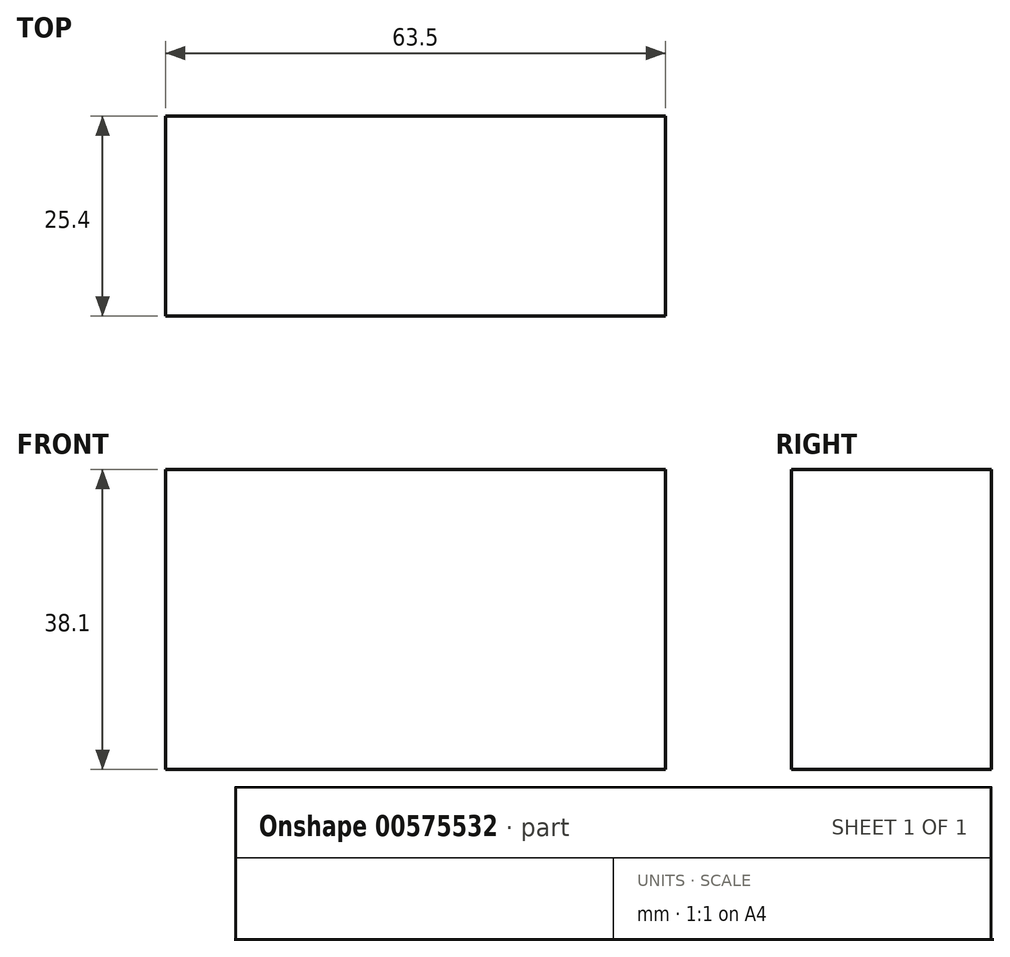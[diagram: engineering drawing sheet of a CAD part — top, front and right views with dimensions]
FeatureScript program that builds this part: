
annotation { "Feature Type Name" : "Feature", "Feature Type Description" : "" }
export const myFeature = defineFeature(function(context is Context, id is Id, definition is map)
    precondition{}
    {
        {
            var Q0;
            Q0=qCreatedBy(makeId("Front.planeOp"),FACE);
            var sketch = newSketch(context, id + "F0", { "sketchPlane" : qUnion([Q0])});
            skLineSegment(sketch, "E0.bottom", {"start": v(-28.07, 21.55) * mm, "end": v(35.43, 21.55) * mm});
            skLineSegment(sketch, "E0.top", {"start": v(-28.07, -16.55) * mm, "end": v(35.43, -16.55) * mm});
            skLineSegment(sketch, "E0.left", {"start": v(-28.07, 21.55) * mm, "end": v(-28.07, -16.55) * mm});
            skLineSegment(sketch, "E0.right", {"start": v(35.43, 21.55) * mm, "end": v(35.43, -16.55) * mm});
            skSolve(sketch);
        }
        {
            var Q0;
            Q0 = qSketchRegion(id + "F0", true);
            extrude(context, id + "F1", {"entities" : qUnion([Q0]), "depth" : 25.4 * mm, "offsetDistance" : 25.4 * mm});
        }
    });
